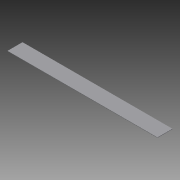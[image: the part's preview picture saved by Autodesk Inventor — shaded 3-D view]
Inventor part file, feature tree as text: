
AUTODESK INVENTOR PART (.ipt)
format: ipt  version: 2013 (Build 170138000, 138)  size: 65,536 bytes
history: native  units: in
note: dims shown in document units (in); Inventor stores cm internally (conversion verified against a paired STEP export)
features: extrude x1, sketch x1
ambient origin geometry x8: Origin, YZ Plane, XZ Plane, XY Plane, X Axis, Y Axis, Z Axis, Center Point
bodies: Solid1 (feature_tree)
feature tree (2):
  extrude  "Extrusion1"  Depth=5.0in
  sketch  "Sketch1"  dims[d0=50.0in d1=5.0in d2=0.125in d3=0.0in]
